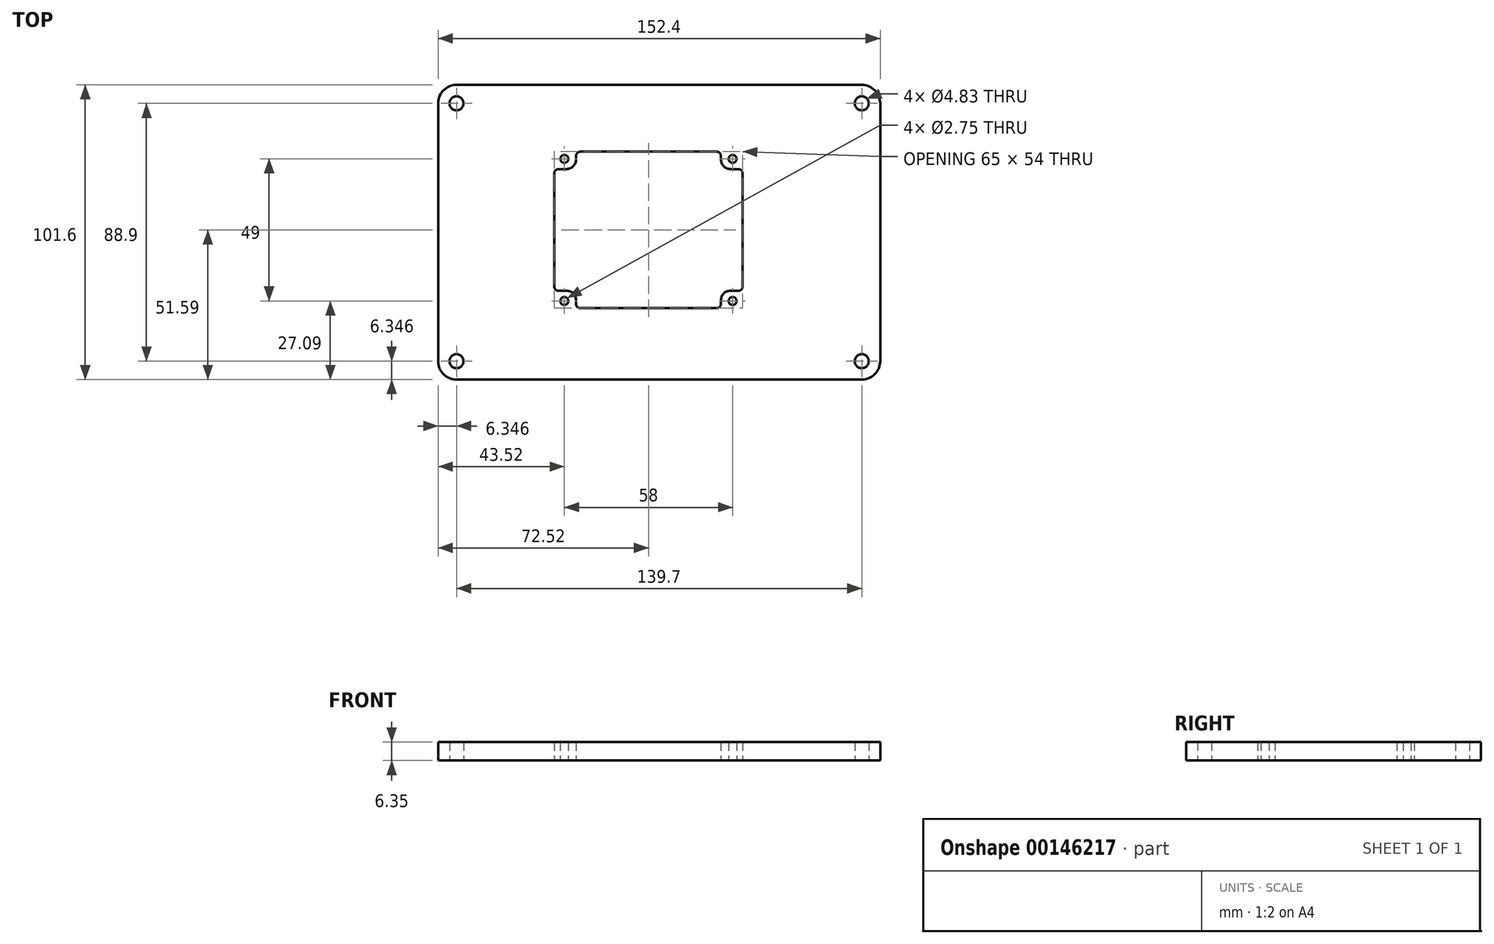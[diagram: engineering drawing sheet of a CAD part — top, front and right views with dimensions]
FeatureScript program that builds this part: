
annotation { "Feature Type Name" : "Feature", "Feature Type Description" : "" }
export const myFeature = defineFeature(function(context is Context, id is Id, definition is map)
    precondition{}
    {
        {
            var Q0;
            Q0=qCreatedBy(makeId("Top.planeOp"),FACE);
            var sketch = newSketch(context, id + "F0", { "sketchPlane" : qUnion([Q0])});
            skLineSegment(sketch, "E0.bottom", {"start": v(-66.17, -51.6) * mm, "end": v(73.53, -51.6) * mm});
            skLineSegment(sketch, "E0.top", {"start": v(-66.17, 50) * mm, "end": v(73.53, 50) * mm});
            skLineSegment(sketch, "E0.left", {"start": v(-72.52, -45.24) * mm, "end": v(-72.52, 43.66) * mm});
            skLineSegment(sketch, "E0.right", {"start": v(79.88, -45.24) * mm, "end": v(79.88, 43.66) * mm});
            skPoint(sketch, "E1.visualSharp", {"position": v(-72.52, 50) * mm});
            skArc(sketch, "E1.filletArc", {"start": v(-66.17, 50) * mm, "mid": v(-70.66, 48.15) * mm, "end": v(-72.52, 43.66) * mm});
            skPoint(sketch, "E2.visualSharp", {"position": v(-72.52, -51.6) * mm});
            skArc(sketch, "E2.filletArc", {"start": v(-72.52, -45.24) * mm, "mid": v(-70.66, -49.73) * mm, "end": v(-66.17, -51.6) * mm});
            skPoint(sketch, "E3.visualSharp", {"position": v(79.88, 50) * mm});
            skArc(sketch, "E3.filletArc", {"start": v(79.88, 43.66) * mm, "mid": v(78.02, 48.15) * mm, "end": v(73.53, 50) * mm});
            skPoint(sketch, "E4.visualSharp", {"position": v(79.88, -51.6) * mm});
            skArc(sketch, "E4.filletArc", {"start": v(73.53, -51.6) * mm, "mid": v(78.02, -49.73) * mm, "end": v(79.88, -45.24) * mm});
            skCircle(sketch, "E5", {"center": v(-66.17, 43.66) * mm, "radius": 2.41 * mm});
            skCircle(sketch, "E6.MirrorC", {"center": v(-66.17, -45.24) * mm, "radius": 2.41 * mm});
            skCircle(sketch, "E7.MirrorC", {"center": v(73.53, 43.66) * mm, "radius": 2.41 * mm});
            skCircle(sketch, "E8.MirrorC", {"center": v(73.53, -45.24) * mm, "radius": 2.41 * mm});
            skPoint(sketch, "E9.middle", {"position": v(0, 0) * mm});
            skCircle(sketch, "E10", {"center": v(-29, 24.5) * mm, "radius": 1.38 * mm});
            skCircle(sketch, "E11", {"center": v(29, 24.5) * mm, "radius": 1.38 * mm});
            skCircle(sketch, "E12.MirrorC", {"center": v(29, -24.5) * mm, "radius": 1.38 * mm});
            skCircle(sketch, "E13.MirrorC", {"center": v(-29, -24.5) * mm, "radius": 1.38 * mm});
            skLineSegment(sketch, "E14.bottom", {"start": v(-30.91, 21) * mm, "end": v(-28.17, 21) * mm});
            skLineSegment(sketch, "E14.top", {"start": v(-30.91, -21) * mm, "end": v(-28.18, -21) * mm});
            skLineSegment(sketch, "E14.left", {"start": v(-32.5, 19.41) * mm, "end": v(-32.5, -19.41) * mm});
            skLineSegment(sketch, "E14.right", {"start": v(32.5, 19.41) * mm, "end": v(32.5, -19.41) * mm});
            skLineSegment(sketch, "E15.bottom", {"start": v(-23.41, 27) * mm, "end": v(23.41, 27) * mm});
            skLineSegment(sketch, "E15.top", {"start": v(-23.41, -27) * mm, "end": v(23.41, -27) * mm});
            skLineSegment(sketch, "E15.left", {"start": v(-25, 25.41) * mm, "end": v(-25, 24.18) * mm});
            skLineSegment(sketch, "E15.right", {"start": v(25, 25.41) * mm, "end": v(25, 24.18) * mm});
            skLineSegment(sketch, "E16.trimOffspring", {"start": v(28.18, 21) * mm, "end": v(30.91, 21) * mm});
            skLineSegment(sketch, "E17.trimOffspring", {"start": v(28.17, -21) * mm, "end": v(30.91, -21) * mm});
            skLineSegment(sketch, "E18.trimOffspring", {"start": v(-25, -24.18) * mm, "end": v(-25, -25.41) * mm});
            skLineSegment(sketch, "E19.trimOffspring", {"start": v(25, -24.18) * mm, "end": v(25, -25.41) * mm});
            skPoint(sketch, "E20.visualSharp", {"position": v(-32.5, 21) * mm});
            skArc(sketch, "E20.filletArc", {"start": v(-30.91, 21) * mm, "mid": v(-32.04, 20.54) * mm, "end": v(-32.5, 19.41) * mm});
            skPoint(sketch, "E21.visualSharp", {"position": v(-25, 21) * mm});
            skArc(sketch, "E21.filletArc", {"start": v(-28.17, 21) * mm, "mid": v(-25.93, 21.93) * mm, "end": v(-25, 24.18) * mm});
            skPoint(sketch, "E22.visualSharp", {"position": v(-25, 27) * mm});
            skArc(sketch, "E22.filletArc", {"start": v(-23.41, 27) * mm, "mid": v(-24.54, 26.54) * mm, "end": v(-25, 25.41) * mm});
            skPoint(sketch, "E23.visualSharp", {"position": v(25, 27) * mm});
            skArc(sketch, "E23.filletArc", {"start": v(25, 25.41) * mm, "mid": v(24.54, 26.54) * mm, "end": v(23.41, 27) * mm});
            skPoint(sketch, "E24.visualSharp", {"position": v(25, 21) * mm});
            skArc(sketch, "E24.filletArc", {"start": v(25, 24.18) * mm, "mid": v(25.93, 21.93) * mm, "end": v(28.18, 21) * mm});
            skPoint(sketch, "E25.visualSharp", {"position": v(-25, -21) * mm});
            skArc(sketch, "E25.filletArc", {"start": v(-25, -24.18) * mm, "mid": v(-25.93, -21.93) * mm, "end": v(-28.18, -21) * mm});
            skPoint(sketch, "E26.visualSharp", {"position": v(25, -21) * mm});
            skArc(sketch, "E26.filletArc", {"start": v(28.17, -21) * mm, "mid": v(25.93, -21.93) * mm, "end": v(25, -24.18) * mm});
            skPoint(sketch, "E27.visualSharp", {"position": v(32.5, -21) * mm});
            skArc(sketch, "E27.filletArc", {"start": v(30.91, -21) * mm, "mid": v(32.04, -20.54) * mm, "end": v(32.5, -19.41) * mm});
            skPoint(sketch, "E28.visualSharp", {"position": v(25, -27) * mm});
            skArc(sketch, "E28.filletArc", {"start": v(23.41, -27) * mm, "mid": v(24.54, -26.54) * mm, "end": v(25, -25.41) * mm});
            skPoint(sketch, "E29.visualSharp", {"position": v(-25, -27) * mm});
            skArc(sketch, "E29.filletArc", {"start": v(-25, -25.41) * mm, "mid": v(-24.54, -26.54) * mm, "end": v(-23.41, -27) * mm});
            skPoint(sketch, "E30.visualSharp", {"position": v(-32.5, -21) * mm});
            skArc(sketch, "E30.filletArc", {"start": v(-32.5, -19.41) * mm, "mid": v(-32.04, -20.54) * mm, "end": v(-30.91, -21) * mm});
            skPoint(sketch, "E31.visualSharp", {"position": v(32.5, 21) * mm});
            skArc(sketch, "E31.filletArc", {"start": v(32.5, 19.41) * mm, "mid": v(32.04, 20.54) * mm, "end": v(30.91, 21) * mm});
            skLineSegment(sketch, "E32", {"start": v(-72.52, -0.8) * mm, "end": v(79.88, -0.8) * mm, "construction": true});
            skLineSegment(sketch, "E33", {"start": v(0, 0) * mm, "end": v(0, -0.8) * mm});
            skSolve(sketch);
        }
        {
            var Q0;
            Q0=makeQuery(id+"F0.imprint","IMPRINT",FACE,{"disambiguationData":[TD([[makeQuery(id+"F0.imprint","IMPRINT",EDGE,{"derivedFrom":sQuery(id+"F0.wireOp",EDGE,"E0.bottom")}),1.0]])]});
            extrude(context, id + "F1", {"entities" : qUnion([Q0]), "depth" : 6.35 * mm});
        }
    });
